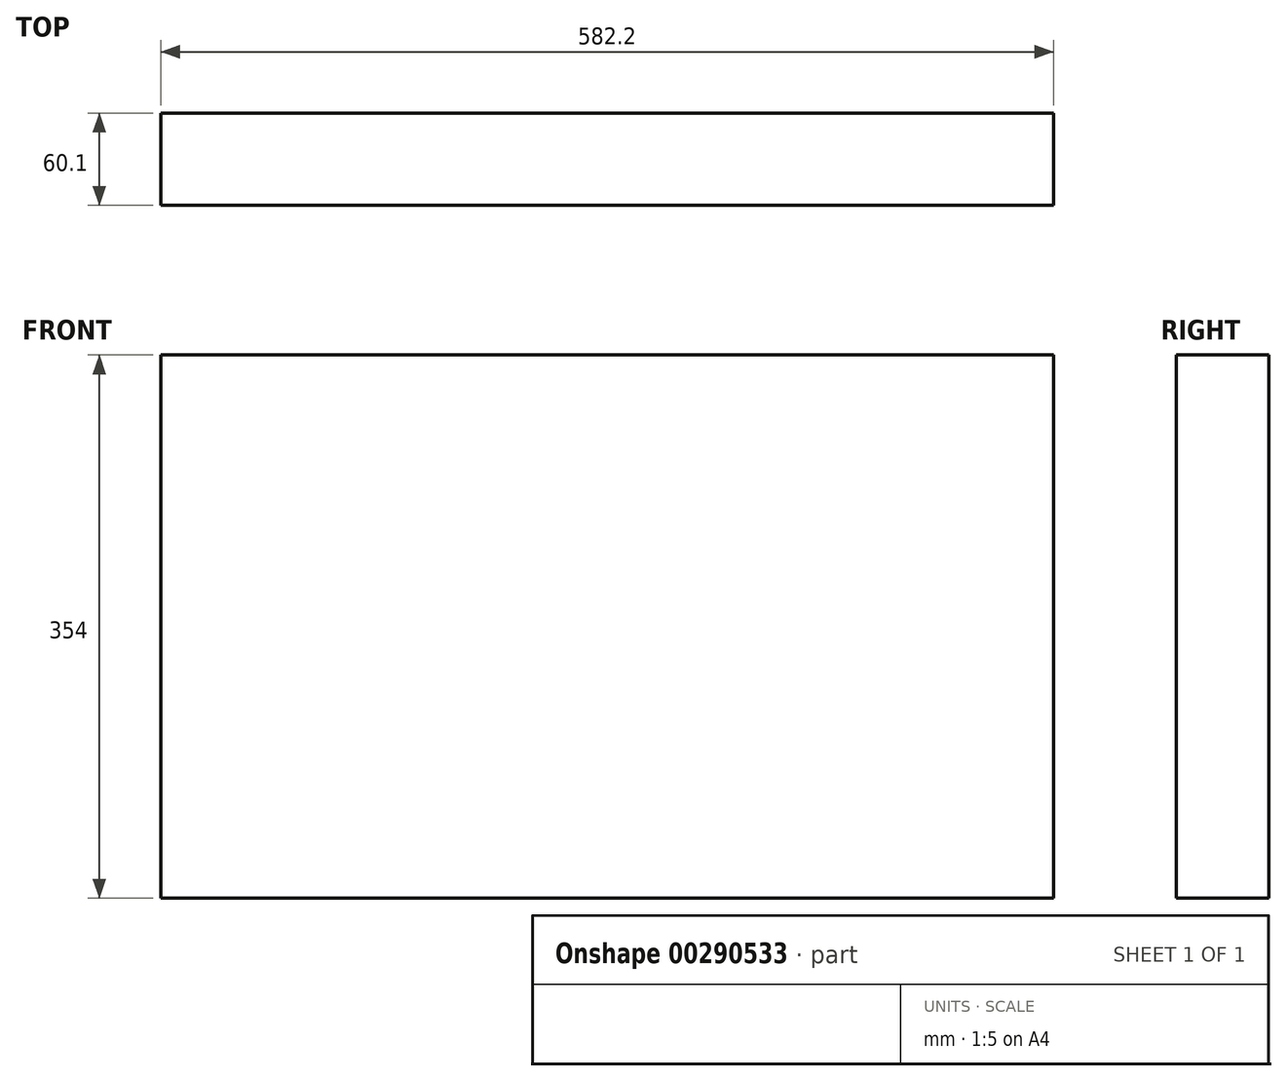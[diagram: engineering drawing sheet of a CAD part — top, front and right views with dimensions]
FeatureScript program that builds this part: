
annotation { "Feature Type Name" : "Feature", "Feature Type Description" : "" }
export const myFeature = defineFeature(function(context is Context, id is Id, definition is map)
    precondition{}
    {
        {
            var Q0;
            Q0=qCreatedBy(makeId("Front.planeOp"),FACE);
            var sketch = newSketch(context, id + "F0", { "sketchPlane" : qUnion([Q0])});
            skLineSegment(sketch, "E0.bottom", {"start": v(291.1, -177) * mm, "end": v(-291.1, -177) * mm});
            skLineSegment(sketch, "E0.top", {"start": v(291.1, 177) * mm, "end": v(-291.1, 177) * mm});
            skLineSegment(sketch, "E0.left", {"start": v(291.1, -177) * mm, "end": v(291.1, 177) * mm});
            skLineSegment(sketch, "E0.right", {"start": v(-291.1, -177) * mm, "end": v(-291.1, 177) * mm});
            skPoint(sketch, "E0.middle", {"position": v(0, 0) * mm});
            skSolve(sketch);
        }
        {
            var Q0;
            Q0 = qSketchRegion(id + "F0", true);
            extrude(context, id + "F1", {"entities" : qUnion([Q0]), "oppositeDirection" : true, "depth" : 60.1 * mm});
        }
    });
